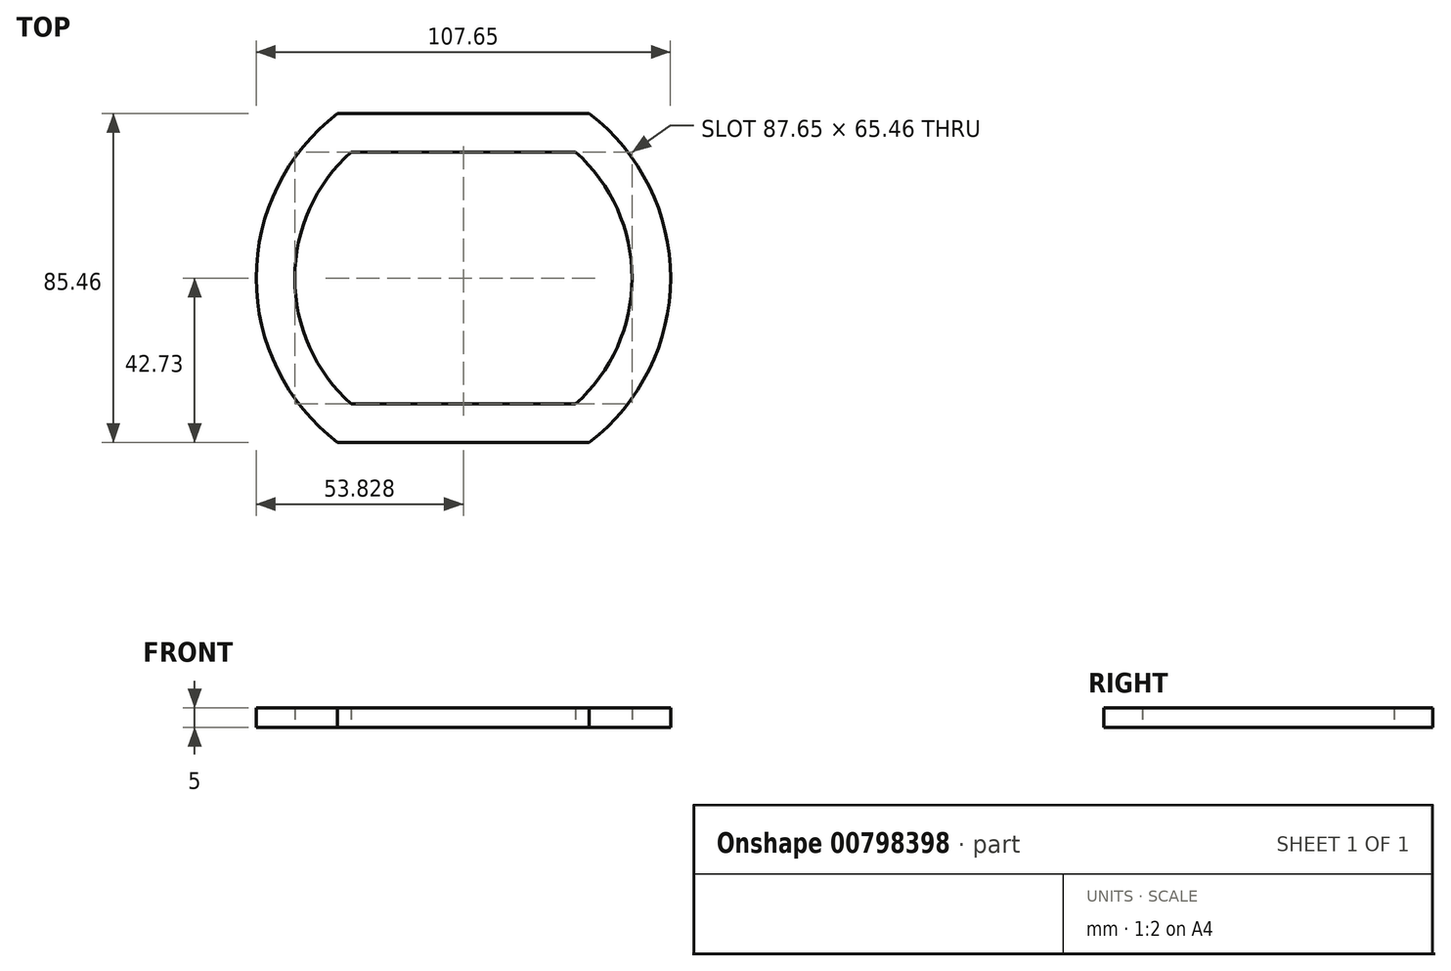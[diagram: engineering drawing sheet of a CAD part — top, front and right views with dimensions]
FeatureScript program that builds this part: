
annotation { "Feature Type Name" : "Feature", "Feature Type Description" : "" }
export const myFeature = defineFeature(function(context is Context, id is Id, definition is map)
    precondition{}
    {
        {
            var Q0;
            Q0=qCreatedBy(makeId("Top.planeOp"),FACE);
            var sketch = newSketch(context, id + "F0", { "sketchPlane" : qUnion([Q0])});
            skLineSegment(sketch, "E0", {"start": v(0, -42.73) * mm, "end": v(-65.46, -42.73) * mm});
            skLineSegment(sketch, "E1", {"start": v(-65.46, 42.73) * mm, "end": v(0, 42.73) * mm});
            skArc(sketch, "E2", {"start": v(0, -42.73) * mm, "mid": v(21.1, 0) * mm, "end": v(0, 42.73) * mm});
            skPoint(sketch, "E2.centerSnap0", {"position": v(-32.73, 42.73) * mm});
            skArc(sketch, "E3.trimOffspring", {"start": v(-65.46, 42.73) * mm, "mid": v(-86.56, 0) * mm, "end": v(-65.46, -42.73) * mm});
            skPoint(sketch, "E4.end.orphan", {"position": v(-65.46, 0) * mm});
            skArc(sketch, "E5.0", {"start": v(-3.59, -32.73) * mm, "mid": v(11.1, 0) * mm, "end": v(-3.59, 32.73) * mm});
            skLineSegment(sketch, "E5.1", {"start": v(-3.59, -32.73) * mm, "end": v(-61.88, -32.73) * mm});
            skArc(sketch, "E5.2", {"start": v(-61.88, 32.73) * mm, "mid": v(-76.56, 0) * mm, "end": v(-61.88, -32.73) * mm});
            skLineSegment(sketch, "E5.3", {"start": v(-61.88, 32.73) * mm, "end": v(-3.59, 32.73) * mm});
            skSolve(sketch);
        }
        {
            var Q0;
            Q0=makeQuery(id+"F0.imprint","IMPRINT",FACE,{"disambiguationData":[TD([[makeQuery(id+"F0.imprint","IMPRINT",EDGE,{"derivedFrom":sQuery(id+"F0.wireOp",EDGE,"E0")}),-1.0]])]});
            extrude(context, id + "F1", {"entities" : qUnion([Q0]), "depth" : 5 * mm, "offsetDistance" : 25 * mm});
        }
    });
